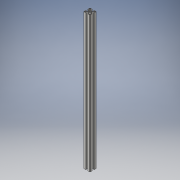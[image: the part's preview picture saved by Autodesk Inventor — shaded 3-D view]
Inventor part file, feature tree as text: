
AUTODESK INVENTOR PART (.ipt)
format: ipt  version: 2016 (Build 200138000, 138)  size: 1,073,152 bytes
history: native  units: in
note: dims shown in document units (in); Inventor stores cm internally (conversion verified against a paired STEP export)
features: extrude x1, sketch x1
ambient origin geometry x8: Origin, YZ Plane, XZ Plane, XY Plane, X Axis, Y Axis, Z Axis, Center Point
bodies: Solid1 (feature_tree)
feature tree (2):
  extrude  "Extrusion1"  [1 undecoded]
  sketch  "Sketch1"  dims[d0=24.8031in d1=0.0in]
note: 1 required parameter value undecoded (feature->parameter linkage not recoverable at this tier; creation-order binding heuristic only, values carry confidence <= 0.55)
